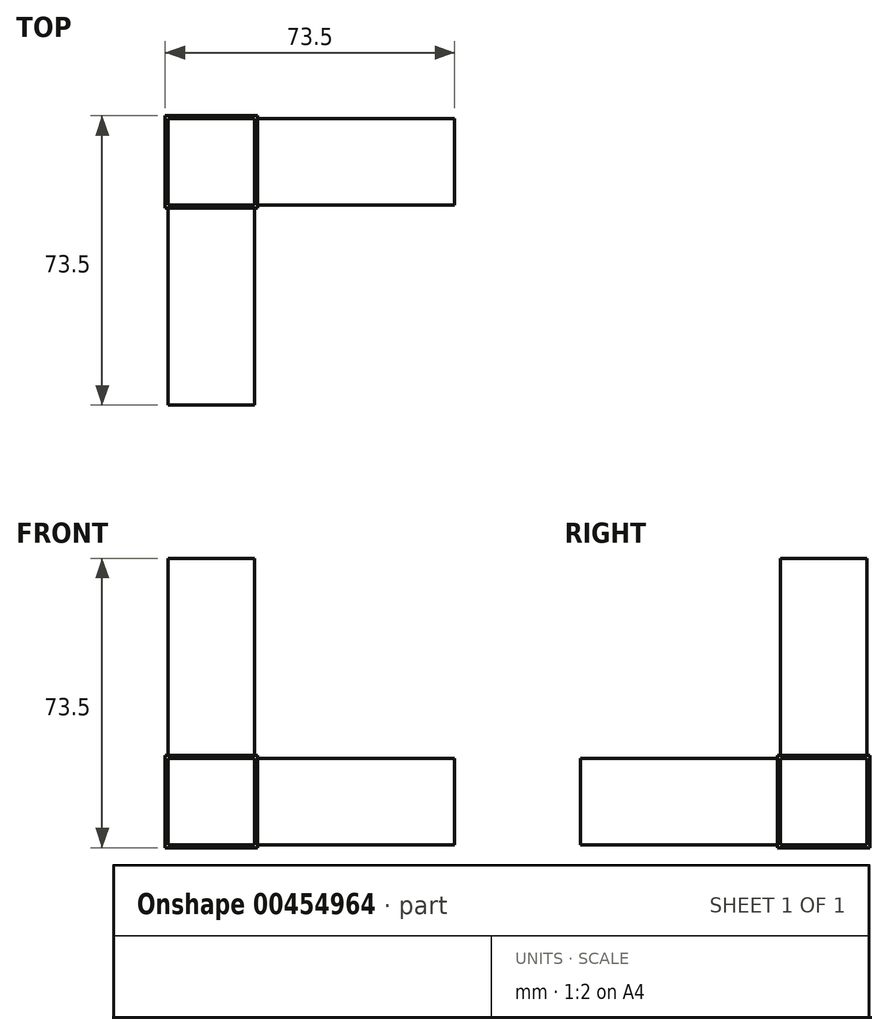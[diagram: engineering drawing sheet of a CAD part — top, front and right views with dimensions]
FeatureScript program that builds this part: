
annotation { "Feature Type Name" : "Feature", "Feature Type Description" : "" }
export const myFeature = defineFeature(function(context is Context, id is Id, definition is map)
    precondition{}
    {
        {
            var Q0;
            Q0=qCreatedBy(makeId("Front.planeOp"),FACE);
            var sketch = newSketch(context, id + "F0", { "sketchPlane" : qUnion([Q0])});
            skLineSegment(sketch, "E0.bottom", {"start": v(11.75, 11.75) * mm, "end": v(-11.75, 11.75) * mm});
            skLineSegment(sketch, "E0.top", {"start": v(11.75, -11.75) * mm, "end": v(-11.75, -11.75) * mm});
            skLineSegment(sketch, "E0.left", {"start": v(11.75, 11.75) * mm, "end": v(11.75, -11.75) * mm});
            skLineSegment(sketch, "E0.right", {"start": v(-11.75, 11.75) * mm, "end": v(-11.75, -11.75) * mm});
            skPoint(sketch, "E0.middle", {"position": v(0, 0) * mm});
            skSolve(sketch);
        }
        {
            var Q0;
            Q0 = qSketchRegion(id + "F0", true);
            extrude(context, id + "F1", {"entities" : qUnion([Q0]), "endBound" : BoundingType.SYMMETRIC, "depth" : 23.5 * mm});
        }
        {
            var Q0;
            Q0=makeQuery(id+"F1.opExtrude","CAP_FACE",FACE,{"disambiguationData":[OSD([sQuery(id+"F0.wireOp",EDGE,"E0.bottom"),sQuery(id+"F0.wireOp",EDGE,"E0.top"),sQuery(id+"F0.wireOp",EDGE,"E0.left"),sQuery(id+"F0.wireOp",EDGE,"E0.right")])],"isStart":false});
            var sketch = newSketch(context, id + "F2", { "sketchPlane" : qUnion([Q0])});
            skLineSegment(sketch, "E1.bottom", {"start": v(11, 11) * mm, "end": v(-11, 11) * mm});
            skLineSegment(sketch, "E1.top", {"start": v(11, -11) * mm, "end": v(-11, -11) * mm});
            skLineSegment(sketch, "E1.left", {"start": v(11, 11) * mm, "end": v(11, -11) * mm});
            skLineSegment(sketch, "E1.right", {"start": v(-11, 11) * mm, "end": v(-11, -11) * mm});
            skPoint(sketch, "E1.middle", {"position": v(0, 0) * mm});
            skSolve(sketch);
        }
        {
            var Q0;
            Q0 = qSketchRegion(id + "F2", true);
            extrude(context, id + "F3", {"entities" : qUnion([Q0]), "operationType" : NewBodyOperationType.ADD, "depth" : 50 * mm});
        }
        {
            var Q0;
            Q0=makeQuery(id+"F1.opExtrude","SWEPT_FACE",FACE,{"disambiguationData":[OSD([sQuery(id+"F0.wireOp",EDGE,"E0.left")])]});
            var sketch = newSketch(context, id + "F4", { "sketchPlane" : qUnion([Q0])});
            skLineSegment(sketch, "E2.bottom", {"start": v(11, 11) * mm, "end": v(-11, 11) * mm});
            skLineSegment(sketch, "E2.top", {"start": v(11, -11) * mm, "end": v(-11, -11) * mm});
            skLineSegment(sketch, "E2.left", {"start": v(11, 11) * mm, "end": v(11, -11) * mm});
            skLineSegment(sketch, "E2.right", {"start": v(-11, 11) * mm, "end": v(-11, -11) * mm});
            skPoint(sketch, "E2.middle", {"position": v(0, 0) * mm});
            skSolve(sketch);
        }
        {
            var Q0;
            Q0 = qSketchRegion(id + "F4", true);
            extrude(context, id + "F5", {"entities" : qUnion([Q0]), "operationType" : NewBodyOperationType.ADD, "depth" : 50 * mm});
        }
        {
            var Q0;
            Q0=makeQuery(id+"F1.opExtrude","SWEPT_FACE",FACE,{"disambiguationData":[OSD([sQuery(id+"F0.wireOp",EDGE,"E0.bottom")])]});
            var sketch = newSketch(context, id + "F6", { "sketchPlane" : qUnion([Q0])});
            skLineSegment(sketch, "E3.bottom", {"start": v(11, 11) * mm, "end": v(-11, 11) * mm});
            skLineSegment(sketch, "E3.top", {"start": v(11, -11) * mm, "end": v(-11, -11) * mm});
            skLineSegment(sketch, "E3.left", {"start": v(11, 11) * mm, "end": v(11, -11) * mm});
            skLineSegment(sketch, "E3.right", {"start": v(-11, 11) * mm, "end": v(-11, -11) * mm});
            skPoint(sketch, "E3.middle", {"position": v(0, 0) * mm});
            skSolve(sketch);
        }
        {
            var Q0;
            Q0 = qSketchRegion(id + "F6", true);
            extrude(context, id + "F7", {"entities" : qUnion([Q0]), "operationType" : NewBodyOperationType.ADD, "depth" : 50 * mm});
        }
    });
